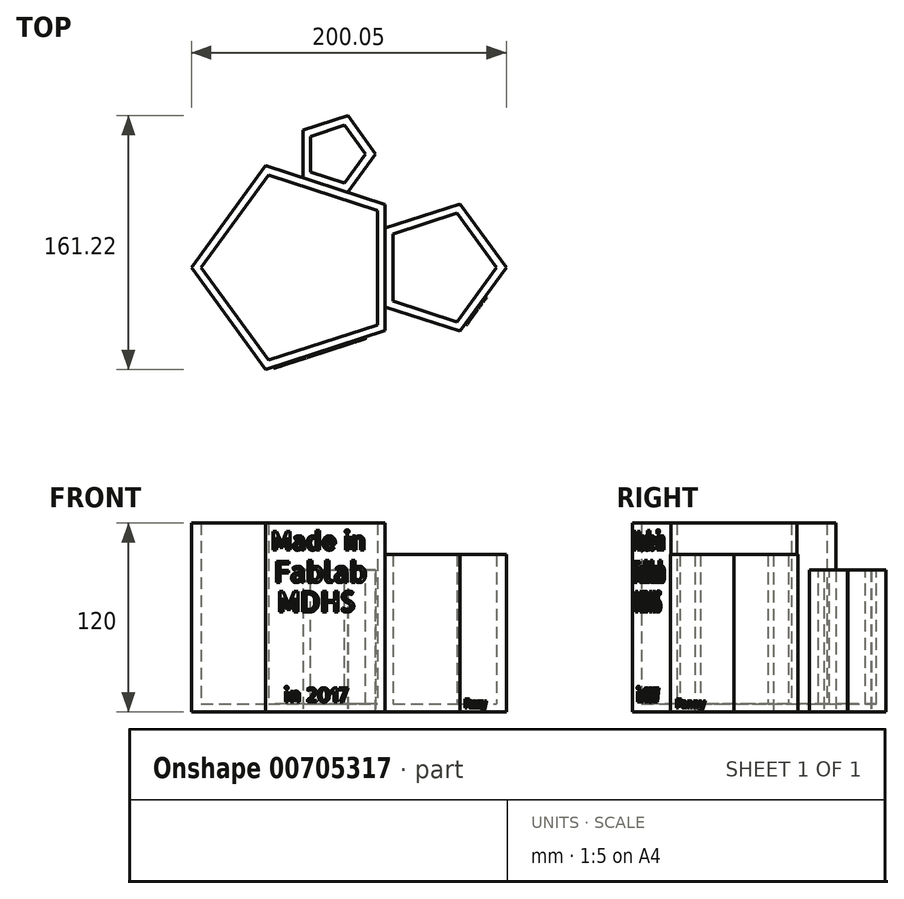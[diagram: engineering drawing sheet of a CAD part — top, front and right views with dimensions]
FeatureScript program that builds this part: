
annotation { "Feature Type Name" : "Feature", "Feature Type Description" : "" }
export const myFeature = defineFeature(function(context is Context, id is Id, definition is map)
    precondition{}
    {
        {
            var Q0;
            Q0=qCreatedBy(makeId("Top.planeOp"),FACE);
            var sketch = newSketch(context, id + "F0", { "sketchPlane" : qUnion([Q0])});
            skCircle(sketch, "E0.cCircle", {"center": v(0, 0) * mm, "radius": 55.06 * mm, "construction": true});
            skLineSegment(sketch, "E0.1", {"start": v(55.06, -40) * mm, "end": v(-21.03, -64.72) * mm});
            skLineSegment(sketch, "E0.2", {"start": v(-21.03, -64.72) * mm, "end": v(-68.05, 0) * mm});
            skLineSegment(sketch, "E0.3", {"start": v(-68.05, 0) * mm, "end": v(-21.03, 64.72) * mm});
            skCircle(sketch, "E1.cCircle", {"center": v(89.46, 0) * mm, "radius": 34.4 * mm, "construction": true});
            skLineSegment(sketch, "E1.0", {"start": v(102.6, 40.45) * mm, "end": v(132, 0) * mm});
            skLineSegment(sketch, "E1.1", {"start": v(132, 0) * mm, "end": v(102.6, -40.45) * mm});
            skLineSegment(sketch, "E1.2", {"start": v(102.6, -40.45) * mm, "end": v(55.06, -25) * mm});
            skLineSegment(sketch, "E1.3", {"start": v(55.06, -25) * mm, "end": v(55.06, 25) * mm});
            skLineSegment(sketch, "E1.4", {"start": v(55.06, 25) * mm, "end": v(102.6, 40.45) * mm});
            skPoint(sketch, "E1.0.midPoint", {"position": v(117.3, 20.23) * mm});
            skLineSegment(sketch, "E2", {"start": v(-21.03, 64.72) * mm, "end": v(55.05, 40) * mm});
            skLineSegment(sketch, "E3", {"start": v(55.05, 40) * mm, "end": v(55.06, -40) * mm});
            skLineSegment(sketch, "E4", {"start": v(55.06, 25) * mm, "end": v(55.06, -25) * mm});
            skSolve(sketch);
        }
        {
            var Q0;
            Q0=makeQuery(id+"F0.imprint","IMPRINT",FACE,{"disambiguationData":[TD([[makeQuery(id+"F0.imprint","IMPRINT",EDGE,{"derivedFrom":sQuery(id+"F0.wireOp",EDGE,"E1.0")}),-1.0]])]});
            var sketch = newSketch(context, id + "F1", { "sketchPlane" : qUnion([Q0])});
            skCircle(sketch, "E5.cCircle", {"center": v(23.48, 72.23) * mm, "radius": 20.65 * mm, "construction": true});
            skLineSegment(sketch, "E5.0", {"start": v(31.37, 47.96) * mm, "end": v(2.84, 57.23) * mm});
            skLineSegment(sketch, "E5.1", {"start": v(2.84, 57.23) * mm, "end": v(2.84, 87.23) * mm});
            skLineSegment(sketch, "E5.2", {"start": v(2.84, 87.23) * mm, "end": v(31.37, 96.5) * mm});
            skLineSegment(sketch, "E5.3", {"start": v(31.37, 96.5) * mm, "end": v(49, 72.23) * mm});
            skLineSegment(sketch, "E5.4", {"start": v(49, 72.23) * mm, "end": v(31.37, 47.96) * mm});
            skSolve(sketch);
        }
        {
            var Q0;
            Q0=makeQuery(id+"F0.imprint","IMPRINT",FACE,{"disambiguationData":[TD([[makeQuery(id+"F0.imprint","IMPRINT",EDGE,{"derivedFrom":sQuery(id+"F0.wireOp",EDGE,"E0.1")}),-1.0]])]});
            extrude(context, id + "F2", {"entities" : qUnion([Q0]), "depth" : 120 * mm, "offsetDistance" : 25 * mm});
        }
        {
            var Q0;
            Q0=makeQuery(id+"F2.opExtrude","CAP_FACE",FACE,{"disambiguationData":[OSD([sQuery(id+"F0.wireOp",EDGE,"E0.1"),sQuery(id+"F0.wireOp",EDGE,"E0.2"),sQuery(id+"F0.wireOp",EDGE,"E0.3"),sQuery(id+"F0.wireOp",EDGE,"E2"),sQuery(id+"F0.wireOp",EDGE,"E3")])],"isStart":false});
            shell(context, id + "F3", {"entities" : qUnion([Q0]), "thickness" : 5 * mm});
        }
        {
            var Q0;
            Q0=makeQuery(id+"F1.imprint","IMPRINT",FACE,{"disambiguationData":[TD([[makeQuery(id+"F1.imprint","IMPRINT",EDGE,{"derivedFrom":makeQuery(id+"F0.imprint","IMPRINT",EDGE,{"derivedFrom":sQuery(id+"F0.wireOp",EDGE,"E1.0")})}),-1.0]])]});
            extrude(context, id + "F4", {"entities" : qUnion([Q0]), "operationType" : NewBodyOperationType.ADD, "depth" : 100 * mm, "offsetDistance" : 25 * mm});
        }
        {
            var Q0;
            Q0=makeQuery(id+"F4.opExtrude","CAP_FACE",FACE,{"disambiguationData":[OSD([sQuery(id+"F0.wireOp",EDGE,"E1.0"),sQuery(id+"F0.wireOp",EDGE,"E1.1"),sQuery(id+"F0.wireOp",EDGE,"E1.2"),sQuery(id+"F0.wireOp",EDGE,"E1.4"),sQuery(id+"F0.wireOp",EDGE,"E4")])],"isStart":false});
            shell(context, id + "F5", {"entities" : qUnion([Q0]), "thickness" : 5 * mm});
        }
        {
            var Q0;
            Q0=makeQuery(id+"F2.opExtrude","SWEPT_FACE",FACE,{"disambiguationData":[OSD([sQuery(id+"F0.wireOp",EDGE,"E0.1")])]});
            var sketch = newSketch(context, id + "F6", { "sketchPlane" : qUnion([Q0])});
            skText(sketch, "E6", { "text": "Made in", "fontName": "AllertaStencil-Regular.ttf"});
            const initialGuessF6  = {"E6": [-0.0362, 0.10275, 1, 0, 0.01171]};
            skSetInitialGuess(sketch, initialGuessF6);
            skSolve(sketch);
        }
        {
            var Q0;
            Q0 = qSketchRegion(id + "F6", true);
            extrude(context, id + "F7", {"entities" : qUnion([Q0]), "operationType" : NewBodyOperationType.ADD, "depth" : 1 * mm, "offsetDistance" : 25 * mm});
        }
        {
            var Q0;
            Q0=makeQuery(id+"F2.opExtrude","SWEPT_FACE",FACE,{"disambiguationData":[OSD([sQuery(id+"F0.wireOp",EDGE,"E0.1")])]});
            var sketch = newSketch(context, id + "F8", { "sketchPlane" : qUnion([Q0])});
            skText(sketch, "E7", { "text": "Fablab", "fontName": "AllertaStencil-Regular.ttf"});
            const initialGuessF8  = {"E7": [-0.0344, 0.08223, 1, 0, 0.01328]};
            skSetInitialGuess(sketch, initialGuessF8);
            skSolve(sketch);
        }
        {
            var Q0;
            Q0 = qSketchRegion(id + "F8", true);
            extrude(context, id + "F9", {"entities" : qUnion([Q0]), "operationType" : NewBodyOperationType.ADD, "depth" : 1 * mm, "offsetDistance" : 25 * mm});
        }
        {
            var Q0;
            Q0=makeQuery(id+"F2.opExtrude","SWEPT_FACE",FACE,{"disambiguationData":[OSD([sQuery(id+"F0.wireOp",EDGE,"E0.1")])]});
            var sketch = newSketch(context, id + "F10", { "sketchPlane" : qUnion([Q0])});
            skText(sketch, "E8", { "text": "MDHS", "fontName": "AllertaStencil-Regular.ttf"});
            const initialGuessF10  = {"E8": [-0.03218, 0.06352, 1, 0, 0.01298]};
            skSetInitialGuess(sketch, initialGuessF10);
            skSolve(sketch);
        }
        {
            var Q0;
            Q0 = qSketchRegion(id + "F10", true);
            extrude(context, id + "F11", {"entities" : qUnion([Q0]), "operationType" : NewBodyOperationType.ADD, "depth" : 1 * mm, "offsetDistance" : 25 * mm});
        }
        {
            var Q0;
            Q0=makeQuery(id+"F2.opExtrude","SWEPT_FACE",FACE,{"disambiguationData":[OSD([sQuery(id+"F0.wireOp",EDGE,"E0.1")])]});
            var sketch = newSketch(context, id + "F12", { "sketchPlane" : qUnion([Q0])});
            skText(sketch, "E9", { "text": "in 2017", "fontName": "AllertaStencil-Regular.ttf"});
            const initialGuessF12  = {"E9": [-0.02773, 0.00618, 1, 0, 0.00905]};
            skSetInitialGuess(sketch, initialGuessF12);
            skSolve(sketch);
        }
        {
            var Q0;
            Q0 = qSketchRegion(id + "F12", true);
            extrude(context, id + "F13", {"entities" : qUnion([Q0]), "operationType" : NewBodyOperationType.ADD, "depth" : 1 * mm, "offsetDistance" : 25 * mm});
        }
        {
            var Q0;
            Q0=makeQuery(id+"F4.opExtrude","SWEPT_FACE",FACE,{"disambiguationData":[OSD([sQuery(id+"F0.wireOp",EDGE,"E1.1")])]});
            var sketch = newSketch(context, id + "F14", { "sketchPlane" : qUnion([Q0])});
            skText(sketch, "E10", { "text": "Fanny", "fontName": "AllertaStencil-Regular.ttf"});
            const initialGuessF14  = {"E10": [0.03214, 0.00267, 1, 0, 0.00544]};
            skSetInitialGuess(sketch, initialGuessF14);
            skSolve(sketch);
        }
        {
            var Q0;
            Q0 = qSketchRegion(id + "F14", true);
            extrude(context, id + "F15", {"entities" : qUnion([Q0]), "operationType" : NewBodyOperationType.ADD, "depth" : 1 * mm, "offsetDistance" : 25 * mm});
        }
        {
            var Q0;
            Q0=qCreatedBy(makeId("Top.planeOp"),FACE);
            var sketch = newSketch(context, id + "F16", { "sketchPlane" : qUnion([Q0])});
            skCircle(sketch, "E11.cCircle", {"center": v(23.4, 72) * mm, "radius": 20.65 * mm, "construction": true});
            skLineSegment(sketch, "E11.0", {"start": v(48.91, 72) * mm, "end": v(31.28, 47.73) * mm});
            skLineSegment(sketch, "E11.1", {"start": v(31.28, 47.73) * mm, "end": v(2.75, 57) * mm});
            skLineSegment(sketch, "E11.2", {"start": v(2.75, 57) * mm, "end": v(2.75, 87) * mm});
            skLineSegment(sketch, "E11.3", {"start": v(2.75, 87) * mm, "end": v(31.28, 96.27) * mm});
            skLineSegment(sketch, "E11.4", {"start": v(31.28, 96.27) * mm, "end": v(48.91, 72) * mm});
            skPoint(sketch, "E11.0.midPoint", {"position": v(40.1, 59.86) * mm});
            skLineSegment(sketch, "E12", {"start": v(23.4, 72) * mm, "end": v(17.01, 52.36) * mm, "construction": true});
            skSolve(sketch);
        }
        {
            var Q0;
            Q0 = qSketchRegion(id + "F1", true);
            var Q1;
            Q1=makeQuery(id+"F16.imprint","IMPRINT",FACE,{"disambiguationData":[TD([[makeQuery(id+"F16.imprint","IMPRINT",EDGE,{"derivedFrom":sQuery(id+"F16.wireOp",EDGE,"E11.0")}),-1.0]])]});
            extrude(context, id + "F17", {"entities" : qUnion([Q0, Q1]), "operationType" : NewBodyOperationType.ADD, "depth" : 90 * mm, "offsetDistance" : 25 * mm});
        }
        {
            var Q0;
            Q0=makeQuery(id+"F17.boolean.opBoolean","MERGE",FACE,{"derivedFrom":[makeQuery(id+"F17.opExtrude","CAP_FACE",FACE,{"disambiguationData":[OSD([sQuery(id+"F1.wireOp",EDGE,"E5.0"),sQuery(id+"F1.wireOp",EDGE,"E5.1"),sQuery(id+"F1.wireOp",EDGE,"E5.2"),sQuery(id+"F1.wireOp",EDGE,"E5.3"),sQuery(id+"F1.wireOp",EDGE,"E5.4")])],"isStart":false}),makeQuery(id+"F17.opExtrude","CAP_FACE",FACE,{"disambiguationData":[OSD([sQuery(id+"F16.wireOp",EDGE,"E11.0"),sQuery(id+"F16.wireOp",EDGE,"E11.1"),sQuery(id+"F16.wireOp",EDGE,"E11.2"),sQuery(id+"F16.wireOp",EDGE,"E11.3"),sQuery(id+"F16.wireOp",EDGE,"E11.4")])],"isStart":false})]});
            var sketch = newSketch(context, id + "F18", { "sketchPlane" : qUnion([Q0])});
            skCircle(sketch, "E13.cCircle", {"center": v(23.4, 72) * mm, "radius": 15.65 * mm, "construction": true});
            skLineSegment(sketch, "E13.0", {"start": v(29.37, 90.39) * mm, "end": v(42.73, 72) * mm});
            skLineSegment(sketch, "E13.1", {"start": v(42.73, 72) * mm, "end": v(29.37, 53.6) * mm});
            skLineSegment(sketch, "E13.2", {"start": v(29.37, 53.6) * mm, "end": v(7.75, 60.63) * mm});
            skLineSegment(sketch, "E13.3", {"start": v(7.75, 60.63) * mm, "end": v(7.75, 83.36) * mm});
            skLineSegment(sketch, "E13.4", {"start": v(7.75, 83.36) * mm, "end": v(29.37, 90.39) * mm});
            skPoint(sketch, "E13.0.midPoint", {"position": v(36.05, 81.2) * mm});
            skSolve(sketch);
        }
        {
            var Q0;
            Q0 = qSketchRegion(id + "F18", true);
            extrude(context, id + "F19", {"entities" : qUnion([Q0]), "operationType" : NewBodyOperationType.REMOVE, "oppositeDirection" : true, "depth" : 85 * mm, "offsetDistance" : 25 * mm});
        }
    });
